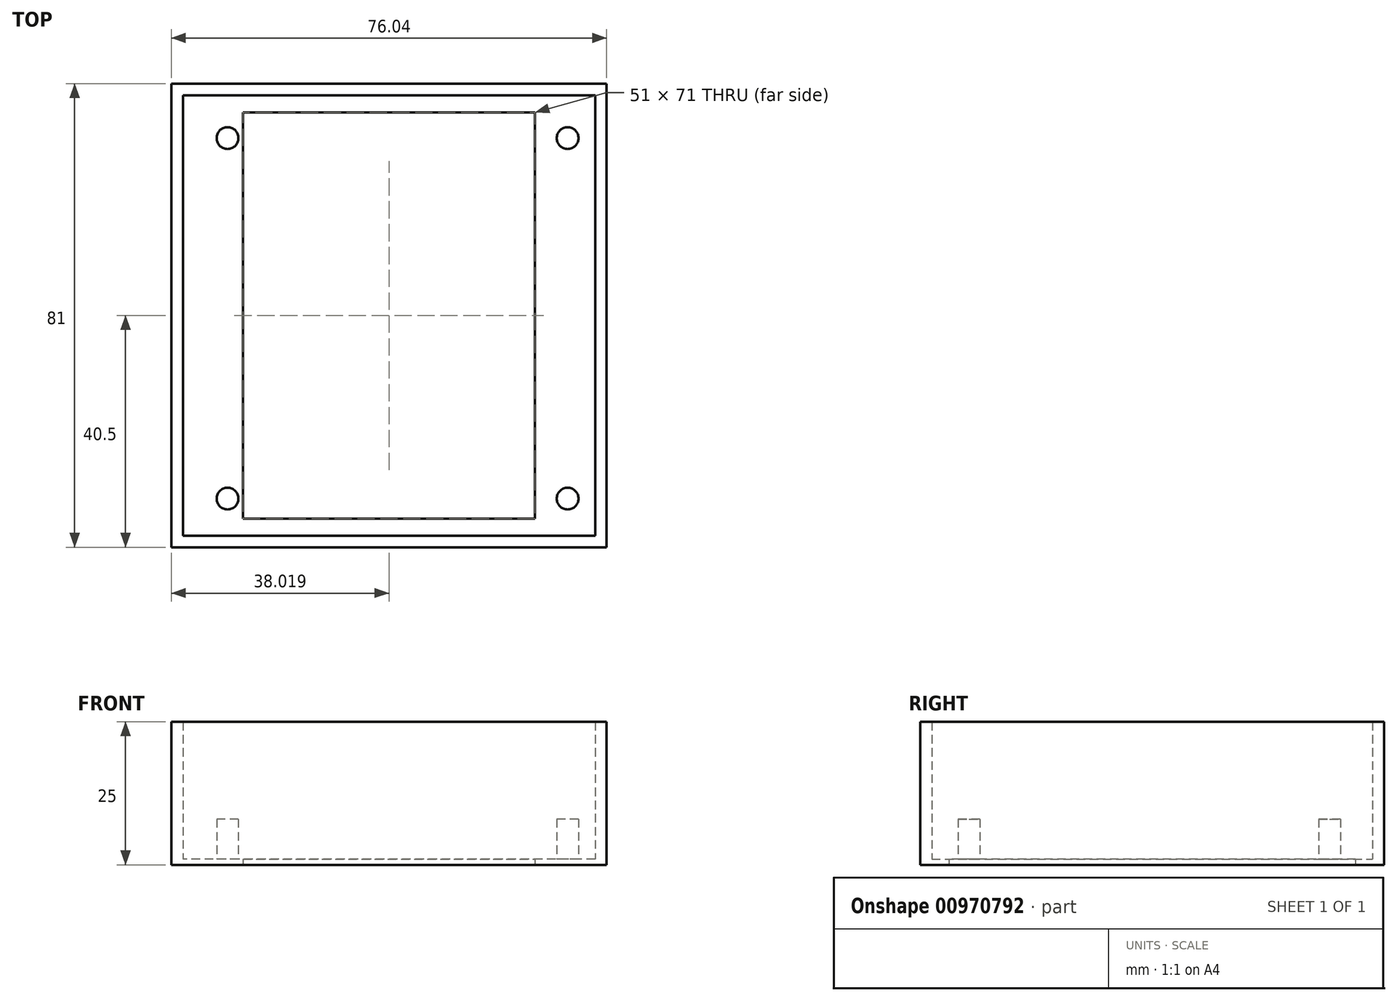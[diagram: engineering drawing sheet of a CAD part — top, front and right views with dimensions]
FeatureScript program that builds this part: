
annotation { "Feature Type Name" : "Feature", "Feature Type Description" : "" }
export const myFeature = defineFeature(function(context is Context, id is Id, definition is map)
    precondition{}
    {
        {
            var Q0;
            Q0=qCreatedBy(makeId("Top.planeOp"),FACE);
            var sketch = newSketch(context, id + "F0", { "sketchPlane" : qUnion([Q0])});
            skLineSegment(sketch, "E0.bottom", {"start": v(-24.8, 35.5) * mm, "end": v(26.2, 35.5) * mm});
            skLineSegment(sketch, "E0.top", {"start": v(-24.8, -35.5) * mm, "end": v(26.2, -35.5) * mm});
            skLineSegment(sketch, "E0.left", {"start": v(-24.8, 35.5) * mm, "end": v(-24.8, -35.5) * mm});
            skLineSegment(sketch, "E0.right", {"start": v(26.2, 35.5) * mm, "end": v(26.2, -35.5) * mm});
            skPoint(sketch, "E0.middle", {"position": v(0.7, 0) * mm});
            skCircle(sketch, "E1", {"center": v(-27.5, 31) * mm, "radius": 1.9 * mm});
            skCircle(sketch, "E2", {"center": v(-27.5, -32) * mm, "radius": 1.9 * mm});
            skCircle(sketch, "E3", {"center": v(31.9, -32) * mm, "radius": 1.9 * mm});
            skCircle(sketch, "E4", {"center": v(31.9, 31) * mm, "radius": 1.9 * mm});
            skLineSegment(sketch, "E5.bottom", {"start": v(-35.3, 38.5) * mm, "end": v(36.7, 38.5) * mm});
            skLineSegment(sketch, "E5.top", {"start": v(-35.3, -38.5) * mm, "end": v(36.7, -38.5) * mm});
            skLineSegment(sketch, "E5.left", {"start": v(-35.3, 38.5) * mm, "end": v(-35.3, -38.5) * mm});
            skLineSegment(sketch, "E5.right", {"start": v(36.7, 38.5) * mm, "end": v(36.7, -38.5) * mm});
            skLineSegment(sketch, "E6.bottom", {"start": v(-37.32, 40.5) * mm, "end": v(38.72, 40.5) * mm});
            skLineSegment(sketch, "E6.top", {"start": v(-37.32, -40.5) * mm, "end": v(38.72, -40.5) * mm});
            skLineSegment(sketch, "E6.left", {"start": v(-37.32, 40.5) * mm, "end": v(-37.32, -40.5) * mm});
            skLineSegment(sketch, "E6.right", {"start": v(38.72, 40.5) * mm, "end": v(38.72, -40.5) * mm});
            skSolve(sketch);
        }
        {
            var Q0;
            Q0=makeQuery(id+"F0.imprint","IMPRINT",FACE,{"disambiguationData":[TD([[makeQuery(id+"F0.imprint","IMPRINT",EDGE,{"derivedFrom":sQuery(id+"F0.wireOp",EDGE,"E5.bottom")}),1.0]])]});
            var Q1;
            Q1=makeQuery(id+"F0.imprint","IMPRINT",FACE,{"disambiguationData":[TD([[makeQuery(id+"F0.imprint","IMPRINT",EDGE,{"derivedFrom":sQuery(id+"F0.wireOp",EDGE,"E0.bottom")}),1.0]])]});
            var Q2;
            Q2=makeQuery(id+"F0.imprint","IMPRINT",FACE,{"disambiguationData":[TD([[makeQuery(id+"F0.imprint","IMPRINT",EDGE,{"derivedFrom":sQuery(id+"F0.wireOp",EDGE,"E4")}),1.0]])]});
            var Q3;
            Q3=makeQuery(id+"F0.imprint","IMPRINT",FACE,{"disambiguationData":[TD([[makeQuery(id+"F0.imprint","IMPRINT",EDGE,{"derivedFrom":sQuery(id+"F0.wireOp",EDGE,"E1")}),1.0]])]});
            var Q4;
            Q4=makeQuery(id+"F0.imprint","IMPRINT",FACE,{"disambiguationData":[TD([[makeQuery(id+"F0.imprint","IMPRINT",EDGE,{"derivedFrom":sQuery(id+"F0.wireOp",EDGE,"E2")}),1.0]])]});
            var Q5;
            Q5=makeQuery(id+"F0.imprint","IMPRINT",FACE,{"disambiguationData":[TD([[makeQuery(id+"F0.imprint","IMPRINT",EDGE,{"derivedFrom":sQuery(id+"F0.wireOp",EDGE,"E3")}),1.0]])]});
            extrude(context, id + "F1", {"entities" : qUnion([Q0, Q1, Q2, Q3, Q4, Q5]), "depth" : 1 * mm, "offsetDistance" : 25 * mm});
        }
        {
            var Q0;
            Q0=makeQuery(id+"F0.imprint","IMPRINT",FACE,{"disambiguationData":[TD([[makeQuery(id+"F0.imprint","IMPRINT",EDGE,{"derivedFrom":sQuery(id+"F0.wireOp",EDGE,"E5.bottom")}),1.0]])]});
            extrude(context, id + "F2", {"entities" : qUnion([Q0]), "operationType" : NewBodyOperationType.ADD, "depth" : 25 * mm, "offsetDistance" : 25 * mm});
        }
        {
            var Q0;
            Q0=makeQuery(id+"F0.imprint","IMPRINT",FACE,{"disambiguationData":[TD([[makeQuery(id+"F0.imprint","IMPRINT",EDGE,{"derivedFrom":sQuery(id+"F0.wireOp",EDGE,"E1")}),1.0]])]});
            var Q1;
            Q1=makeQuery(id+"F0.imprint","IMPRINT",FACE,{"disambiguationData":[TD([[makeQuery(id+"F0.imprint","IMPRINT",EDGE,{"derivedFrom":sQuery(id+"F0.wireOp",EDGE,"E4")}),1.0]])]});
            var Q2;
            Q2=makeQuery(id+"F0.imprint","IMPRINT",FACE,{"disambiguationData":[TD([[makeQuery(id+"F0.imprint","IMPRINT",EDGE,{"derivedFrom":sQuery(id+"F0.wireOp",EDGE,"E2")}),1.0]])]});
            var Q3;
            Q3=makeQuery(id+"F0.imprint","IMPRINT",FACE,{"disambiguationData":[TD([[makeQuery(id+"F0.imprint","IMPRINT",EDGE,{"derivedFrom":sQuery(id+"F0.wireOp",EDGE,"E3")}),1.0]])]});
            extrude(context, id + "F3", {"entities" : qUnion([Q0, Q1, Q2, Q3]), "operationType" : NewBodyOperationType.ADD, "depth" : 8 * mm, "offsetDistance" : 25 * mm});
        }
    });
